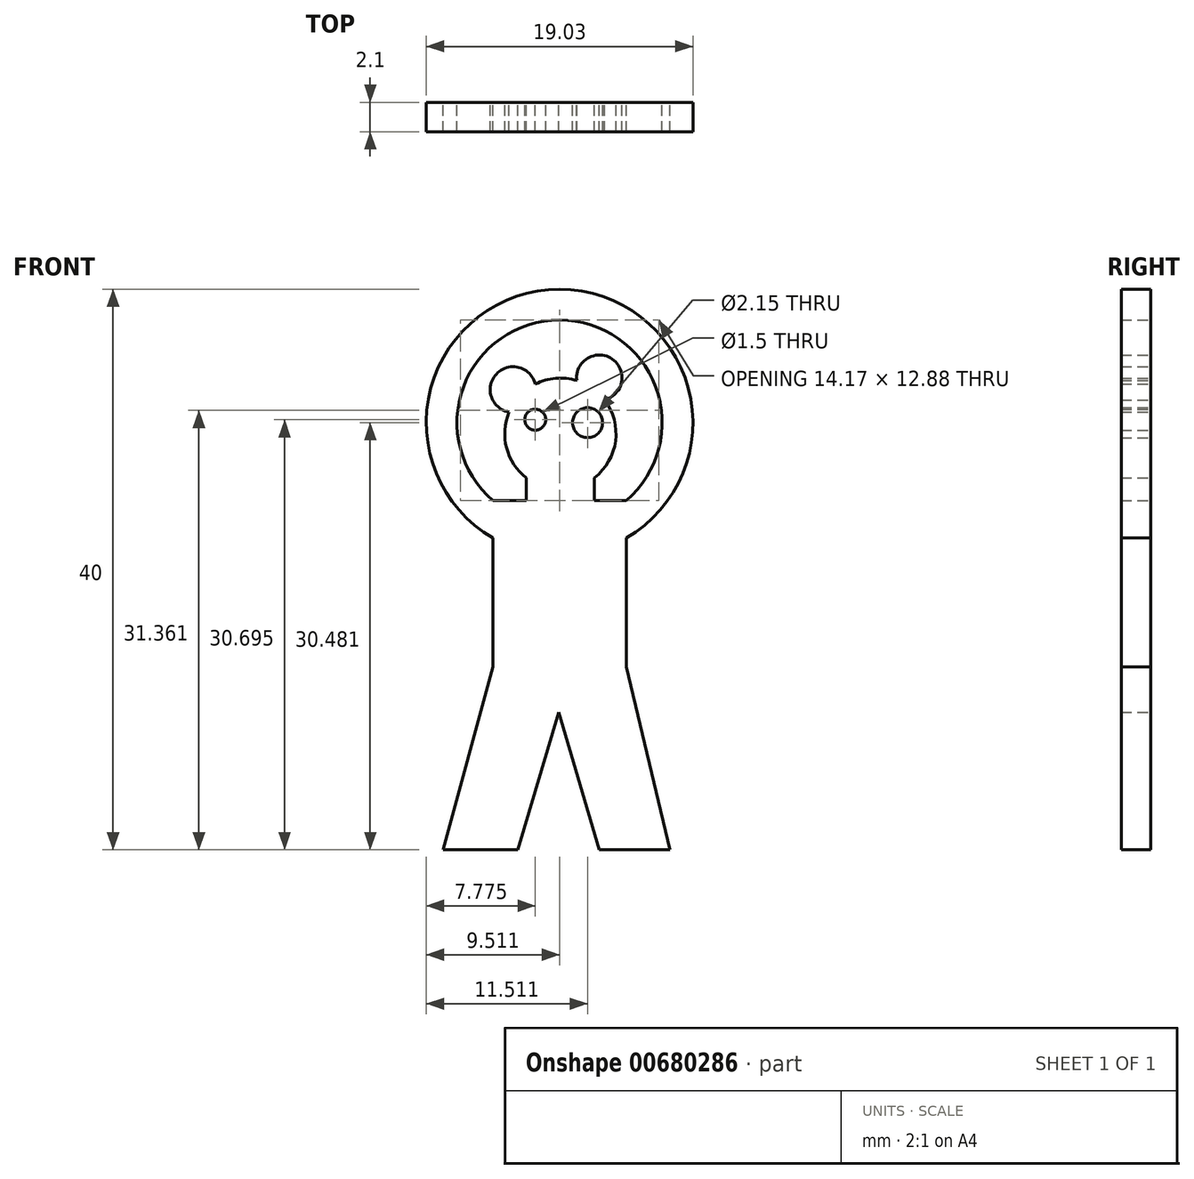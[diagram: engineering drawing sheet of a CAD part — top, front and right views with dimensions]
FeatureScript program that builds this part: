
annotation { "Feature Type Name" : "Feature", "Feature Type Description" : "" }
export const myFeature = defineFeature(function(context is Context, id is Id, definition is map)
    precondition{}
    {
        {
            var Q0;
            Q0=qCreatedBy(makeId("Front.planeOp"),FACE);
            var sketch = newSketch(context, id + "F0", { "sketchPlane" : qUnion([Q0])});
            skLineSegment(sketch, "E0.bottom", {"start": v(-20.2, 7.64) * mm, "end": v(-15.36, 7.64) * mm});
            skLineSegment(sketch, "E0.top", {"start": v(-20.2, 6.02) * mm, "end": v(-15.36, 6.02) * mm});
            skLineSegment(sketch, "E0.left", {"start": v(-20.2, 7.64) * mm, "end": v(-20.2, 6.02) * mm});
            skLineSegment(sketch, "E0.right", {"start": v(-15.36, 7.64) * mm, "end": v(-15.36, 6.02) * mm});
            skLineSegment(sketch, "E1", {"start": v(-20.2, 6.02) * mm, "end": v(-22.6, 6.02) * mm});
            skLineSegment(sketch, "E2", {"start": v(-22.6, 6.02) * mm, "end": v(-22.6, -5.86) * mm});
            skLineSegment(sketch, "E3", {"start": v(-22.6, -5.86) * mm, "end": v(-13.08, -5.86) * mm});
            skLineSegment(sketch, "E4", {"start": v(-13.08, -5.86) * mm, "end": v(-13.08, 6.02) * mm});
            skLineSegment(sketch, "E5", {"start": v(-15.36, 6.02) * mm, "end": v(-13.08, 6.02) * mm});
            skArc(sketch, "E6", {"start": v(-13.08, 6.02) * mm, "mid": v(-17.84, 18.9) * mm, "end": v(-22.6, 6.02) * mm});
            skArc(sketch, "E7", {"start": v(-13.08, 3.34) * mm, "mid": v(-17.84, 21.1) * mm, "end": v(-22.6, 3.34) * mm});
            skLineSegment(sketch, "E8", {"start": v(-22.6, -5.86) * mm, "end": v(-26.16, -18.9) * mm});
            skLineSegment(sketch, "E9", {"start": v(-26.16, -18.9) * mm, "end": v(-20.81, -18.9) * mm});
            skLineSegment(sketch, "E10", {"start": v(-20.81, -18.9) * mm, "end": v(-17.9, -9.08) * mm});
            skLineSegment(sketch, "E11", {"start": v(-17.9, -9.08) * mm, "end": v(-15, -18.9) * mm});
            skLineSegment(sketch, "E12", {"start": v(-15, -18.9) * mm, "end": v(-9.97, -18.9) * mm});
            skLineSegment(sketch, "E13", {"start": v(-9.97, -18.9) * mm, "end": v(-13.08, -5.86) * mm});
            skArc(sketch, "E14", {"start": v(-15.36, 7.64) * mm, "mid": v(-17.78, 14.76) * mm, "end": v(-20.2, 7.64) * mm});
            skArc(sketch, "E15", {"start": v(-14.63, 13.2) * mm, "mid": v(-14.07, 16.12) * mm, "end": v(-16.6, 14.59) * mm});
            skArc(sketch, "E16", {"start": v(-19.58, 14.34) * mm, "mid": v(-22.35, 15.05) * mm, "end": v(-21.44, 12.33) * mm});
            skCircle(sketch, "E17", {"center": v(-19.58, 11.8) * mm, "radius": 0.75 * mm});
            skCircle(sketch, "E18", {"center": v(-15.84, 11.58) * mm, "radius": 1.07 * mm});
            skFitSpline(sketch, "E19", {"points": [v(-19.1, 8.86) * mm, v(-18.17, 8.66) * mm, v(-17.04, 8.66) * mm, v(-15.77, 8.86) * mm, v(-15.7, 8.86) * mm], "startDerivative": vector(3.28, -0.82) * mm, "endDerivative": vector(0.57, -0.08) * mm});
            skSolve(sketch);
        }
        {
            var Q0;
            Q0 = qSketchRegion(id + "F0", true);
            var Q1;
            Q1=makeQuery(id+"F0.imprint","IMPRINT",FACE,{"disambiguationData":[TD([[makeQuery(id+"F0.imprint","IMPRINT",EDGE,{"derivedFrom":sQuery(id+"F0.wireOp",EDGE,"E0.bottom")}),-1.0]])]});
            var Q2;
            {var subQ0=sQuery(id+"F0.wireOp",EDGE,"E16");Q2=makeQuery(id+"F0.imprint","IMPRINT",FACE,{"disambiguationData":[TD([[makeQuery(id+"F0.imprint","IMPRINT",EDGE,{"derivedFrom":subQ0}),1.0]])]});}
            var Q3;
            {var subQ0=sQuery(id+"F0.wireOp",EDGE,"E15");Q3=makeQuery(id+"F0.imprint","IMPRINT",FACE,{"disambiguationData":[TD([[makeQuery(id+"F0.imprint","IMPRINT",EDGE,{"derivedFrom":subQ0}),1.0]])]});}
            var Q4;
            {var subQ5=sQuery(id+"F0.wireOp",EDGE,"E0.bottom");Q4=makeQuery(id+"F0.imprint","IMPRINT",FACE,{"disambiguationData":[TD([[makeQuery(id+"F0.imprint","IMPRINT",EDGE,{"derivedFrom":subQ5}),1.0]])]});}
            extrude(context, id + "F1", {"entities" : qUnion([Q0, Q1, Q2, Q3, Q4]), "depth" : 2.1 * mm, "offsetDistance" : 25 * mm});
        }
    });
